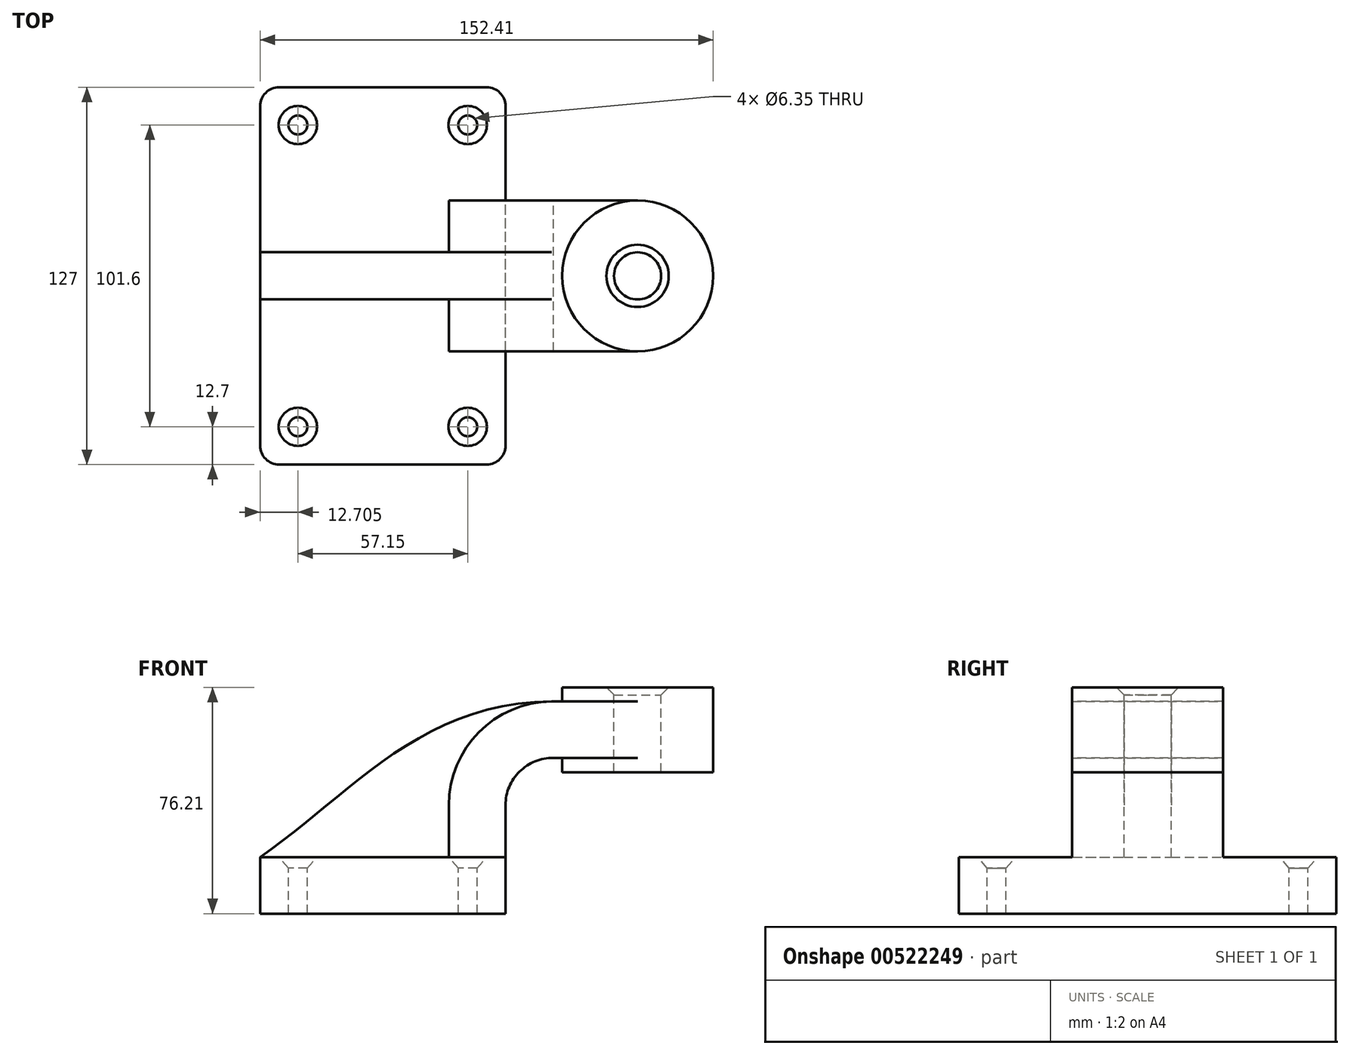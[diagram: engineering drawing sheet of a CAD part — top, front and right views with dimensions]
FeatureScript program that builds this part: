
annotation { "Feature Type Name" : "Feature", "Feature Type Description" : "" }
export const myFeature = defineFeature(function(context is Context, id is Id, definition is map)
    precondition{}
    {
        {
            var Q0;
            Q0=qCreatedBy(makeId("Front.planeOp"),FACE);
            var sketch = newSketch(context, id + "F0", { "sketchPlane" : qUnion([Q0])});
            skLineSegment(sketch, "E0.bottom", {"start": v(41.28, -9.52) * mm, "end": v(-41.28, -9.53) * mm});
            skLineSegment(sketch, "E0.top", {"start": v(41.28, 9.53) * mm, "end": v(-41.28, 9.53) * mm});
            skLineSegment(sketch, "E0.left", {"start": v(41.28, -9.52) * mm, "end": v(41.28, 9.53) * mm});
            skLineSegment(sketch, "E0.right", {"start": v(-41.28, -9.53) * mm, "end": v(-41.28, 9.53) * mm});
            skPoint(sketch, "E0.middle", {"position": v(0, 0) * mm});
            skLineSegment(sketch, "E1", {"start": v(41.28, 9.53) * mm, "end": v(41.28, 27) * mm});
            skLineSegment(sketch, "E2.bottom", {"start": v(111.12, 66.68) * mm, "end": v(60.32, 66.68) * mm});
            skLineSegment(sketch, "E2.top", {"start": v(111.12, 38.1) * mm, "end": v(60.33, 38.1) * mm});
            skLineSegment(sketch, "E2.left", {"start": v(111.12, 66.68) * mm, "end": v(111.12, 38.1) * mm});
            skLineSegment(sketch, "E2.right", {"start": v(60.32, 66.68) * mm, "end": v(60.32, 38.1) * mm});
            skPoint(sketch, "E2.middle", {"position": v(85.72, 52.39) * mm});
            skPoint(sketch, "E2.middle.positionSnap0", {"position": v(57.15, 52.39) * mm});
            skPoint(sketch, "E2.centerSnap0", {"position": v(57.15, 52.39) * mm});
            skLineSegment(sketch, "E3", {"start": v(57.4, 42.88) * mm, "end": v(85.72, 42.88) * mm});
            skArc(sketch, "E4", {"start": v(41.27, 27) * mm, "mid": v(46.01, 38.32) * mm, "end": v(57.4, 42.88) * mm});
            skLineSegment(sketch, "E5.1", {"start": v(22.23, 9.53) * mm, "end": v(22.23, 27) * mm});
            skLineSegment(sketch, "E6.0", {"start": v(57.52, 61.93) * mm, "end": v(85.72, 61.93) * mm});
            skLineSegment(sketch, "E7", {"start": v(85.72, 61.93) * mm, "end": v(85.72, 42.88) * mm});
            skArc(sketch, "E8.0", {"start": v(22.23, 27) * mm, "mid": v(32.59, 51.83) * mm, "end": v(57.52, 61.93) * mm});
            skFitSpline(sketch, "E9", {"points": [v(-41.28, 9.53) * mm, v(57.52, 61.93) * mm], "startDerivative": vector(86.62, 58.98) * mm, "endDerivative": vector(135.69, -0.48) * mm});
            skLineSegment(sketch, "E10", {"start": v(85.72, 66.68) * mm, "end": v(85.72, 38.1) * mm});
            skSolve(sketch);
        }
        {
            var Q0;
            Q0=makeQuery(id+"F0.imprint","IMPRINT",FACE,{"disambiguationData":[TD([[makeQuery(id+"F0.imprint","IMPRINT",EDGE,{"derivedFrom":sQuery(id+"F0.wireOp",EDGE,"E0.bottom")}),-1.0]])]});
            extrude(context, id + "F1", {"entities" : qUnion([Q0]), "endBound" : BoundingType.SYMMETRIC, "depth" : 127 * mm, "offsetDistance" : 25.4 * mm});
        }
        {
            var Q0;
            {var subQ0=sQuery(id+"F0.wireOp",EDGE,"E6.0");var subQ1=sQuery(id+"F0.wireOp",EDGE,"E2.right");var subQ2=makeQuery(id+"F0.imprint","INTERSECT",VERTEX,{"derivedFrom":[subQ1,subQ0]});Q0=makeQuery(id+"F0.imprint","IMPRINT",FACE,{"disambiguationData":[TD([[makeQuery(id+"F0.imprint","IMPRINT",EDGE,{"disambiguationData":[TD([[subQ2,-1.0]])],"derivedFrom":subQ1}),1.0]])]});}
            var Q1;
            {var subQ6=sQuery(id+"F0.wireOp",EDGE,"E1");Q1=makeQuery(id+"F0.imprint","IMPRINT",FACE,{"disambiguationData":[TD([[makeQuery(id+"F0.imprint","IMPRINT",EDGE,{"derivedFrom":subQ6}),1.0]])]});}
            extrude(context, id + "F2", {"entities" : qUnion([Q0, Q1]), "operationType" : NewBodyOperationType.ADD, "endBound" : BoundingType.SYMMETRIC, "depth" : 50.8 * mm, "offsetDistance" : 25.4 * mm});
        }
        {
            var Q0;
            {var subQ3=sQuery(id+"F0.wireOp",EDGE,"E5.1");Q0=makeQuery(id+"F0.imprint","IMPRINT",FACE,{"disambiguationData":[TD([[makeQuery(id+"F0.imprint","IMPRINT",EDGE,{"derivedFrom":subQ3}),1.0]])]});}
            extrude(context, id + "F3", {"entities" : qUnion([Q0]), "operationType" : NewBodyOperationType.ADD, "endBound" : BoundingType.SYMMETRIC, "depth" : 15.88 * mm, "offsetDistance" : 25.4 * mm});
        }
        {
            var Q0;
            {var subQ0=sQuery(id+"F0.wireOp",EDGE,"E2.left");Q0=makeQuery(id+"F0.imprint","IMPRINT",FACE,{"disambiguationData":[TD([[makeQuery(id+"F0.imprint","IMPRINT",EDGE,{"derivedFrom":subQ0}),-1.0]])]});}
            var Q1;
            Q1=sQuery(id+"F0.wireOp",EDGE,"E10");
            revolve(context, id + "F4", {"operationType" : NewBodyOperationType.ADD, "entities" : qUnion([Q0]), "axis" : qUnion([Q1]), "revolveType" : RevolveType.FULL});
        }
        {
            var Q0;
            Q0=makeQuery(id+"F1.opExtrude","CAP_EDGE",EDGE,{"disambiguationData":[OSD([sQuery(id+"F0.wireOp",EDGE,"E0.left")])],"isStart":false});
            var Q1;
            Q1=makeQuery(id+"F1.opExtrude","CAP_EDGE",EDGE,{"disambiguationData":[OSD([sQuery(id+"F0.wireOp",EDGE,"E0.right")])],"isStart":false});
            var Q2;
            Q2=makeQuery(id+"F1.opExtrude","CAP_EDGE",EDGE,{"disambiguationData":[OSD([sQuery(id+"F0.wireOp",EDGE,"E0.right")])],"isStart":true});
            var Q3;
            Q3=makeQuery(id+"F1.opExtrude","CAP_EDGE",EDGE,{"disambiguationData":[OSD([sQuery(id+"F0.wireOp",EDGE,"E0.left")])],"isStart":true});
            fillet(context, id + "F5", {"entities" : qUnion([Q0, Q1, Q2, Q3]), "radius" : 6.35 * mm, "tangentPropagation" : true, "allowEdgeOverflow" : false});
        }
        {
            var Q0;
            Q0=makeQuery(id+"F4.opRevolve","SWEPT_FACE",FACE,{"disambiguationData":[OSD([sQuery(id+"F0.wireOp",EDGE,"E2.bottom")])]});
            var sketch = newSketch(context, id + "F6", { "sketchPlane" : qUnion([Q0])});
            skCircle(sketch, "E11", {"center": v(85.72, 0) * mm, "radius": 7.94 * mm});
            skSolve(sketch);
        }
        {
            var Q0;
            Q0 = qSketchRegion(id + "F6", true);
            extrude(context, id + "F7", {"entities" : qUnion([Q0]), "operationType" : NewBodyOperationType.REMOVE, "endBound" : BoundingType.SYMMETRIC, "oppositeDirection" : true, "depth" : 76.2 * mm, "offsetDistance" : 25.4 * mm});
        }
        {
            var Q0;
            Q0=makeQuery(id+"F7.boolean.opBoolean","INTERSECT",EDGE,{"derivedFrom":[makeQuery(id+"F4.opRevolve","SWEPT_FACE",FACE,{"disambiguationData":[OSD([sQuery(id+"F0.wireOp",EDGE,"E2.bottom")])]}),makeQuery(id+"F7.opExtrude","SWEPT_FACE",FACE,{"disambiguationData":[OSD([sQuery(id+"F6.wireOp",EDGE,"E11")])]})]});
            chamfer(context, id + "F8", {"entities" : qUnion([Q0]), "width" : 2.54 * mm, "tangentPropagation" : true});
        }
        {
            var Q0;
            {var subQ4=sQuery(id+"F0.wireOp",EDGE,"E0.top");var subQ5=sQuery(id+"F0.wireOp",EDGE,"E0.right");var subQ6=sQuery(id+"F0.wireOp",EDGE,"E0.left");Q0=makeQuery(id+"F3.boolean.opBoolean","SPLIT",FACE,{"disambiguationData":[TD([makeQuery(id+"F1.opExtrude","CAP_FACE",FACE,{"disambiguationData":[OSD([sQuery(id+"F0.wireOp",EDGE,"E0.bottom"),subQ4,subQ6,subQ5])],"isStart":true})])],"derivedFrom":makeQuery(id+"F1.opExtrude","SWEPT_FACE",FACE,{"disambiguationData":[OSD([subQ4])]})});}
            var sketch = newSketch(context, id + "F9", { "sketchPlane" : qUnion([Q0])});
            skPoint(sketch, "E12", {"position": v(-28.58, 50.8) * mm});
            skPoint(sketch, "E13", {"position": v(28.58, 50.8) * mm});
            skPoint(sketch, "E14", {"position": v(28.58, -50.8) * mm});
            skPoint(sketch, "E15", {"position": v(-28.58, -50.8) * mm});
            skSolve(sketch);
        }
        {
            var Q0;
            Q0=sQuery(id+"F9.wireOp",VERTEX,"E12");
            var Q1;
            Q1=sQuery(id+"F9.wireOp",VERTEX,"E13");
            var Q2;
            Q2=sQuery(id+"F9.wireOp",VERTEX,"E14");
            var Q3;
            Q3=sQuery(id+"F9.wireOp",VERTEX,"E15");
            var Q4;
            Q4=makeQuery(id+"F1.opExtrude","SWEPT_BODY",BODY,{"disambiguationData":[OSD([sQuery(id+"F0.wireOp",EDGE,"E0.bottom"),sQuery(id+"F0.wireOp",EDGE,"E0.top"),sQuery(id+"F0.wireOp",EDGE,"E0.left"),sQuery(id+"F0.wireOp",EDGE,"E0.right")])]});
            hole(context, id + "F10", {"style" : HoleStyle.C_SINK, "endStyle" : HoleEndStyle.THROUGH, "holeDiameter" : 6.35 * mm, "cSinkDiameter" : 12.88 * mm, "cSinkAngle" : 82 * degree, "isTappedThrough" : true, "tappedDepth" : 12.7 * mm, "tapClearance" : 3, "locations" : qUnion([Q0, Q1, Q2, Q3]), "scope" : qUnion([Q4])});
        }
    });
